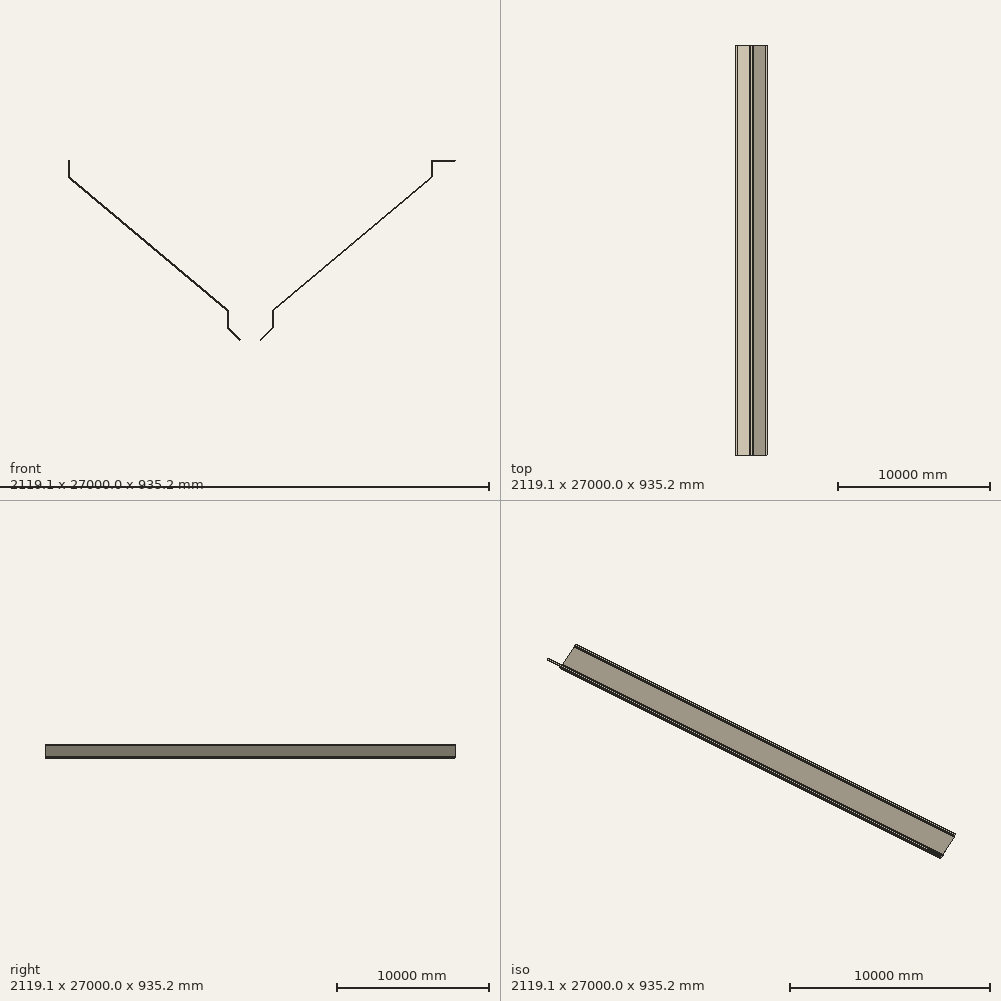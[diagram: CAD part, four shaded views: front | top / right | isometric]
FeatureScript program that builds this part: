
annotation { "Feature Type Name" : "Feature", "Feature Type Description" : "" }
export const myFeature = defineFeature(function(context is Context, id is Id, definition is map)
    precondition{}
    {
        {
            var Q0;
            Q0=qCreatedBy(makeId("Front.planeOp"),FACE);
            var sketch = newSketch(context, id + "F0", { "sketchPlane" : qUnion([Q0])});
            skLineSegment(sketch, "E0", {"start": v(-1084, 2.96) * mm, "end": v(-1084, -87.04) * mm});
            skLineSegment(sketch, "E1", {"start": v(-1084, -87.04) * mm, "end": v(-263.2, -775.77) * mm});
            skLineSegment(sketch, "E2", {"start": v(-263.2, -862.81) * mm, "end": v(-263.2, -775.77) * mm});
            skLineSegment(sketch, "E3", {"start": v(-263.2, -862.81) * mm, "end": v(-197.8, -928.22) * mm});
            skLineSegment(sketch, "E4", {"start": v(-197.8, -928.22) * mm, "end": v(-149.45, -928.22) * mm});
            skLineSegment(sketch, "E5", {"start": v(-1084, 2.96) * mm, "end": v(-1209, 2.96) * mm});
            skLineSegment(sketch, "E6.0", {"start": v(-1088, -88.9) * mm, "end": v(-267.2, -777.64) * mm});
            skLineSegment(sketch, "E7.0", {"start": v(-1088, -1.04) * mm, "end": v(-1088, -88.9) * mm});
            skLineSegment(sketch, "E8.0", {"start": v(-1088, -1.04) * mm, "end": v(-1209, -1.04) * mm});
            skLineSegment(sketch, "E9", {"start": v(-1209, 2.96) * mm, "end": v(-1209, -1.04) * mm});
            skLineSegment(sketch, "E10.0", {"start": v(-267.2, -864.47) * mm, "end": v(-199.45, -932.22) * mm});
            skLineSegment(sketch, "E11", {"start": v(-267.2, -777.64) * mm, "end": v(-267.2, -864.47) * mm});
            skLineSegment(sketch, "E12.0", {"start": v(-199.45, -932.22) * mm, "end": v(-149.45, -932.22) * mm});
            skLineSegment(sketch, "E13.MirrorCS", {"start": v(910.1, 0) * mm, "end": v(910.1, -4) * mm});
            skLineSegment(sketch, "E14.MirrorCS", {"start": v(785.1, 0) * mm, "end": v(910.1, 0) * mm});
            skLineSegment(sketch, "E15.MirrorCS", {"start": v(785.1, 0) * mm, "end": v(785.1, -87.04) * mm});
            skLineSegment(sketch, "E16.MirrorCS", {"start": v(-31.7, -864.47) * mm, "end": v(-99.45, -932.22) * mm});
            skLineSegment(sketch, "E17.MirrorCS", {"start": v(-35.7, -862.81) * mm, "end": v(-101.1, -928.22) * mm});
            skLineSegment(sketch, "E18.MirrorCS", {"start": v(-99.45, -932.22) * mm, "end": v(-149.45, -932.22) * mm});
            skLineSegment(sketch, "E19.MirrorCS", {"start": v(-101.1, -928.22) * mm, "end": v(-149.45, -928.22) * mm});
            skLineSegment(sketch, "E20.MirrorCS", {"start": v(789.1, -4) * mm, "end": v(789.1, -88.9) * mm});
            skLineSegment(sketch, "E21.MirrorCS", {"start": v(789.1, -4) * mm, "end": v(910.1, -4) * mm});
            skLineSegment(sketch, "E22.MirrorCS", {"start": v(-35.7, -862.81) * mm, "end": v(-35.7, -775.77) * mm});
            skLineSegment(sketch, "E23.MirrorCS", {"start": v(-31.7, -777.64) * mm, "end": v(-31.7, -864.47) * mm});
            skLineSegment(sketch, "E24.MirrorCS", {"start": v(789.1, -88.9) * mm, "end": v(-31.7, -777.64) * mm});
            skLineSegment(sketch, "E25.MirrorCS", {"start": v(785.1, -87.04) * mm, "end": v(-35.7, -775.77) * mm});
            skSolve(sketch);
        }
        {
            var Q0;
            Q0=makeQuery(id+"F0.imprint","IMPRINT",FACE,{"disambiguationData":[TD([[makeQuery(id+"F0.imprint","IMPRINT",EDGE,{"derivedFrom":sQuery(id+"F0.wireOp",EDGE,"E0")}),-1.0]])]});
            extrude(context, id + "F1", {"entities" : qUnion([Q0]), "depth" : 27000 * mm});
        }
    });
